# Revit family: Rohrschelle
name_source: partatom
category: Generic Models
revit_build: Autodesk Revit 2015 (Build: 20140606_1530(x64)
units: mm (PartAtom-declared; Revit-internal decimal feet)

## types (11) — shared parameters
Manufacturer = OBO Bettermann
Material = Hot-dip galvanised
SW = 13 mm
URL = http://www.obo-bettermann.com

## per-type parameters (varying)
| type | GTIN | Height | Height 1 | Height 2 | Height 3 | Length | Length 1 | Length 2 | Manufacturer Art.No. | Radius | Radius 1 | Radius 2 | Width | Width 1 |
| 303 DIN-3/8 | 4012195399797 | 3 mm  [stored 0.00984252 ft] | 9 mm  [stored 0.0295276 ft] | 11 mm  [stored 0.0360892 ft] | 16 mm  [stored 0.0524934 ft] | 39 mm  [stored 0.127953 ft] | 69 mm | 27 mm | 5102057 | 9 mm  [stored 0.0295276 ft] | 12 mm  [stored 0.0393701 ft] | 4 mm  [stored 0.0131234 ft] | 9 mm  [stored 0.0295276 ft] | 8 mm  [stored 0.0262467 ft] |
| 303 DIN-1/2 | 4012195399858 | 3 mm  [stored 0.00984252 ft] | 9 mm  [stored 0.0295276 ft] | 11 mm  [stored 0.0360892 ft] | 16 mm  [stored 0.0524934 ft] | 41 mm  [stored 0.134514 ft] | 71 mm | 29 mm  [stored 0.0951444 ft] | 5102073 | 11 mm  [stored 0.0360892 ft] | 14 mm  [stored 0.0459318 ft] | 4 mm  [stored 0.0131234 ft] | 11 mm  [stored 0.0360892 ft] | 10 mm  [stored 0.0328084 ft] |
| 303 DIN-3/4 | 4012195399919 | 3 mm  [stored 0.00984252 ft] | 9 mm  [stored 0.0295276 ft] | 11 mm  [stored 0.0360892 ft] | 16 mm  [stored 0.0524934 ft] | 44 mm  [stored 0.144357 ft] | 74 mm | 32 mm  [stored 0.104987 ft] | 5102081 | 14 mm  [stored 0.0459318 ft] | 17 mm | 4 mm  [stored 0.0131234 ft] | 15 mm  [stored 0.0492126 ft] | 12 mm  [stored 0.0393701 ft] |
| 303 DIN-1 | 4012195399971 | 3 mm  [stored 0.00984252 ft] | 9 mm  [stored 0.0295276 ft] | 11 mm  [stored 0.0360892 ft] | 16 mm  [stored 0.0524934 ft] | 47 mm | 77 mm | 35 mm | 5102111 | 17 mm | 20 mm  [stored 0.0656168 ft] | 4 mm  [stored 0.0131234 ft] | 18 mm | 16 mm  [stored 0.0524934 ft] |
| 303 DIN-1 1/4 | 4012195400035 | 3 mm  [stored 0.00984252 ft] | 9 mm  [stored 0.0295276 ft] | 11 mm  [stored 0.0360892 ft] | 16 mm  [stored 0.0524934 ft] | 52 mm | 82 mm | 40 mm  [stored 0.131234 ft] | 5102138 | 21 mm | 24 mm | 4 mm  [stored 0.0131234 ft] | 22 mm | 19 mm  [stored 0.062336 ft] |
| 303 DIN-1 1/2 | 4012195400097 | 3 mm  [stored 0.00984252 ft] | 9 mm  [stored 0.0295276 ft] | 11 mm  [stored 0.0360892 ft] | 16 mm  [stored 0.0524934 ft] | 55 mm | 85 mm | 43 mm  [stored 0.141076 ft] | 5102154 | 24 mm | 27 mm | 4 mm  [stored 0.0131234 ft] | 25 mm  [stored 0.082021 ft] | 24 mm |
| 303 DIN-2 | 4012195400158 | 3 mm  [stored 0.00984252 ft] | 9 mm  [stored 0.0295276 ft] | 11 mm  [stored 0.0360892 ft] | 16 mm  [stored 0.0524934 ft] | 61 mm | 91 mm | 49 mm  [stored 0.160761 ft] | 5102197 | 30 mm | 33 mm | 4 mm  [stored 0.0131234 ft] | 31 mm  [stored 0.101706 ft] | 29 mm  [stored 0.0951444 ft] |
| 303 DIN-2 1/2 | 4012195400219 | 3 mm  [stored 0.00984252 ft] | 9 mm  [stored 0.0295276 ft] | 11 mm  [stored 0.0360892 ft] | 16 mm  [stored 0.0524934 ft] | 69 mm | 99 mm | 57 mm | 5102219 | 38 mm | 41 mm  [stored 0.134514 ft] | 4 mm  [stored 0.0131234 ft] | 39 mm  [stored 0.127953 ft] | 37 mm  [stored 0.121391 ft] |
| 303 DIN-3 | 4012195400271 | 3 mm  [stored 0.00984252 ft] | 9 mm  [stored 0.0295276 ft] | 11 mm  [stored 0.0360892 ft] | 16 mm  [stored 0.0524934 ft] | 75 mm | 105 mm | 63 mm | 5102235 | 45 mm  [stored 0.147638 ft] | 48 mm | 4 mm  [stored 0.0131234 ft] | 45 mm  [stored 0.147638 ft] | 44 mm  [stored 0.144357 ft] |
| 303 DIN-3 1/2 | 4012195400332 | 3 mm  [stored 0.00984252 ft] | 9 mm  [stored 0.0295276 ft] | 11 mm  [stored 0.0360892 ft] | 16 mm  [stored 0.0524934 ft] | 81 mm | 111 mm | 69 mm | 5102251 | 50 mm  [stored 0.164042 ft] | 53 mm | 4 mm  [stored 0.0131234 ft] | 51 mm | 49 mm  [stored 0.160761 ft] |
| 303 DIN-4 | 4012195400394 | 4 mm  [stored 0.0131234 ft] | 11 mm  [stored 0.0360892 ft] | 13 mm | 25 mm  [stored 0.082021 ft] | 89 mm | 119 mm | 77 mm | 5102278 | 57 mm | 61 mm | 5 mm  [stored 0.0164042 ft] | 58 mm | 56 mm |

note: column(s) folded — value = type name in every type: Article Type

note: [stored X ft] marks values corroborated as IEEE doubles in the binary element streams (Revit-internal decimal feet)

## geometry (parser evidence)
native form markers: Sweep x2
no freeform markers — native parametric forms only
